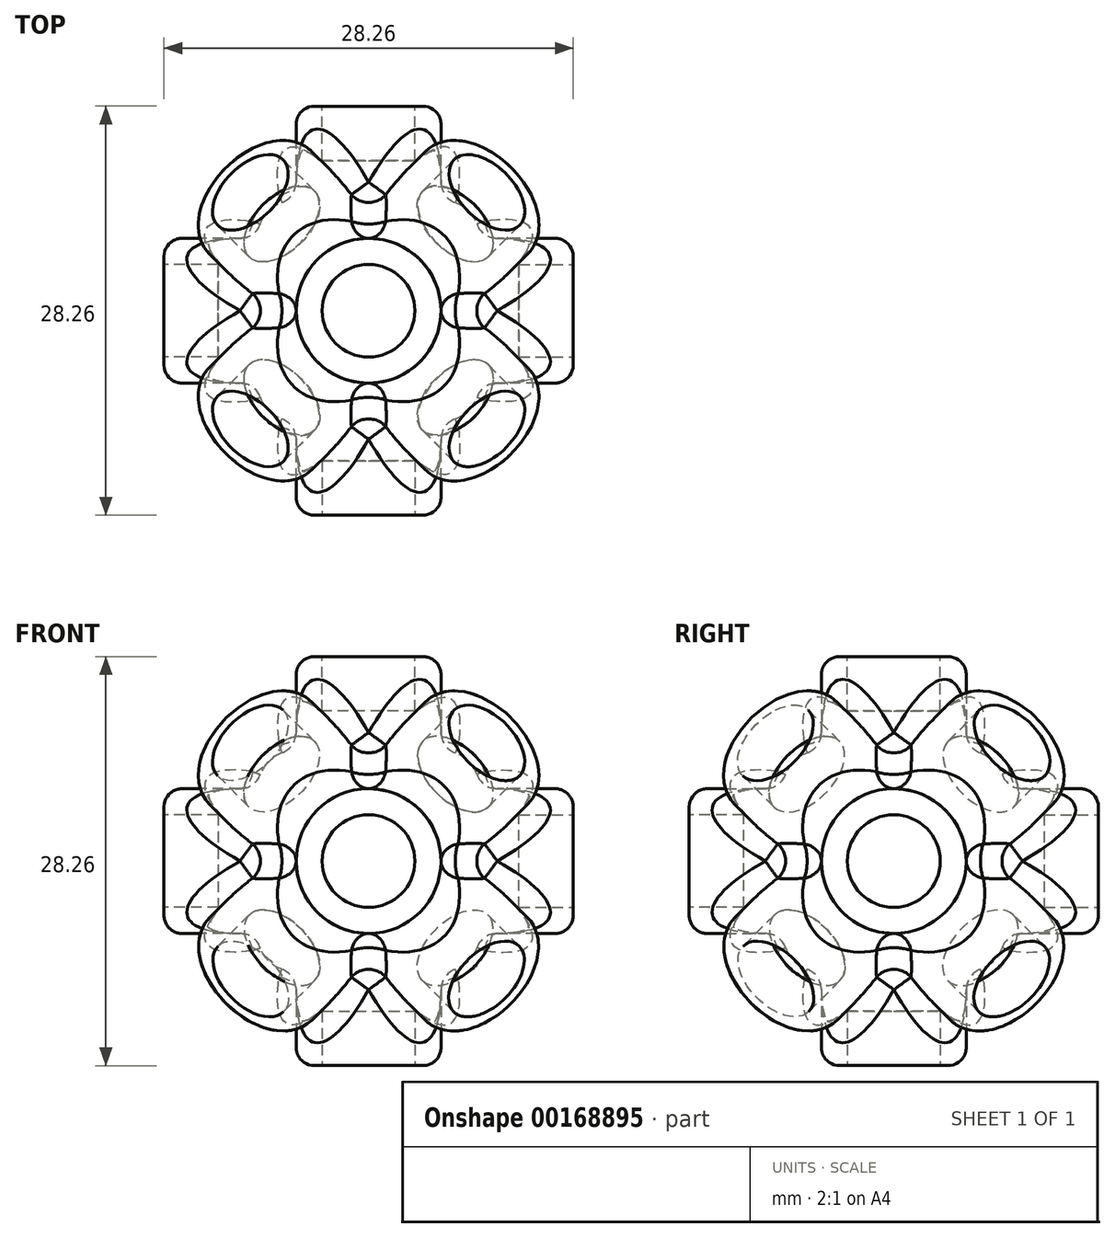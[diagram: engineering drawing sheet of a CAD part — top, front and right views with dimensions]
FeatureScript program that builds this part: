
annotation { "Feature Type Name" : "Feature", "Feature Type Description" : "" }
export const myFeature = defineFeature(function(context is Context, id is Id, definition is map)
    precondition{}
    {
        {
            var Q0;
            Q0=qCreatedBy(makeId("Top.planeOp"),FACE);
            var sketch = newSketch(context, id + "F0", { "sketchPlane" : qUnion([Q0])});
            skCircle(sketch, "E0", {"center": v(0, 0) * mm, "radius": 5 * mm});
            skSolve(sketch);
        }
        {
            var Q0;
            Q0=makeQuery(id+"F0.imprint","IMPRINT",FACE,{"disambiguationData":[TD([[makeQuery(id+"F0.imprint","IMPRINT",EDGE,{"derivedFrom":sQuery(id+"F0.wireOp",EDGE,"E0")}),1.0]])]});
            extrude(context, id + "F1", {"entities" : qUnion([Q0]), "endBound" : BoundingType.SYMMETRIC, "depth" : 28.25 * mm});
        }
        {
            var Q0;
            Q0=qCreatedBy(makeId("Right.planeOp"),FACE);
            var sketch = newSketch(context, id + "F2", { "sketchPlane" : qUnion([Q0])});
            skCircle(sketch, "E1", {"center": v(0, 0) * mm, "radius": 5 * mm});
            skSolve(sketch);
        }
        {
            var Q0;
            Q0=makeQuery(id+"F2.imprint","IMPRINT",FACE,{"disambiguationData":[TD([[makeQuery(id+"F2.imprint","IMPRINT",EDGE,{"derivedFrom":sQuery(id+"F2.wireOp",EDGE,"E1")}),1.0]])]});
            extrude(context, id + "F3", {"entities" : qUnion([Q0]), "operationType" : NewBodyOperationType.ADD, "endBound" : BoundingType.SYMMETRIC, "depth" : 28.25 * mm});
        }
        {
            var Q0;
            Q0=qCreatedBy(makeId("Front.planeOp"),FACE);
            var sketch = newSketch(context, id + "F4", { "sketchPlane" : qUnion([Q0])});
            skCircle(sketch, "E2", {"center": v(0, 0) * mm, "radius": 5 * mm});
            skSolve(sketch);
        }
        {
            var Q0;
            Q0=makeQuery(id+"F4.imprint","IMPRINT",FACE,{"disambiguationData":[TD([[makeQuery(id+"F4.imprint","IMPRINT",EDGE,{"derivedFrom":sQuery(id+"F4.wireOp",EDGE,"E2")}),1.0]])]});
            extrude(context, id + "F5", {"entities" : qUnion([Q0]), "operationType" : NewBodyOperationType.ADD, "endBound" : BoundingType.SYMMETRIC, "depth" : 28.25 * mm});
        }
        {
            var Q0;
            {var subQ0=sQuery(id+"F0.wireOp",EDGE,"E0");var subQ1=makeQuery(id+"F1.opExtrude","SWEPT_FACE",FACE,{"disambiguationData":[OSD([subQ0])]});Q0=makeQuery(id+"F5.boolean.opBoolean","INTERSECT",EDGE,{"disambiguationData":[OD(1.0)],"derivedFrom":[makeQuery(id+"F3.boolean.opBoolean","SPLIT",FACE,{"disambiguationData":[TD([makeQuery(id+"F1.opExtrude","CAP_FACE",FACE,{"disambiguationData":[OSD([subQ0])],"isStart":false})])],"derivedFrom":subQ1}),makeQuery(id+"F5.opExtrude","SWEPT_FACE",FACE,{"disambiguationData":[OSD([sQuery(id+"F4.wireOp",EDGE,"E2")])]})]});}
            cPoint(context, id + "F6", {"entities" : qUnion([Q0]), "parameter" : 0.5});
        }
        {
            var Q0;
            Q0=makeQuery(id+"F3.boolean.opBoolean","INTERSECT",EDGE,{"disambiguationData":[OD(3.0)],"derivedFrom":[makeQuery(id+"F1.opExtrude","SWEPT_FACE",FACE,{"disambiguationData":[OSD([sQuery(id+"F0.wireOp",EDGE,"E0")])]}),makeQuery(id+"F3.opExtrude","SWEPT_FACE",FACE,{"disambiguationData":[OSD([sQuery(id+"F2.wireOp",EDGE,"E1")])]})]});
            cPoint(context, id + "F7", {"entities" : qUnion([Q0]), "parameter" : 0.5});
        }
        {
            var Q0;
            {var subQ0=sQuery(id+"F2.wireOp",EDGE,"E1");var subQ1=makeQuery(id+"F3.opExtrude","SWEPT_FACE",FACE,{"disambiguationData":[OSD([subQ0])]});Q0=makeQuery(id+"F5.boolean.opBoolean","INTERSECT",EDGE,{"disambiguationData":[OD(1.0)],"derivedFrom":[makeQuery(id+"F3.boolean.opBoolean","SPLIT",FACE,{"disambiguationData":[TD([makeQuery(id+"F3.opExtrude","CAP_FACE",FACE,{"disambiguationData":[OSD([subQ0])],"isStart":false})])],"derivedFrom":subQ1}),makeQuery(id+"F5.opExtrude","SWEPT_FACE",FACE,{"disambiguationData":[OSD([sQuery(id+"F4.wireOp",EDGE,"E2")])]})]});}
            cPoint(context, id + "F8", {"entities" : qUnion([Q0]), "parameter" : 0.5});
        }
        {
            var Q0;
            Q0 = qCreatedBy(id + "F6" ,VERTEX);
            var Q1;
            Q1 = qCreatedBy(id + "F7" ,VERTEX);
            var Q2;
            Q2 = qCreatedBy(id + "F8" ,VERTEX);
            cPlane(context, id + "F9", {"entities" : qUnion([Q0, Q1, Q2]), "cplaneType" : CPlaneType.THREE_POINT, "offset" : 25 * mm, "width" : 150 * mm, "height" : 150 * mm});
        }
        {
            var Q0;
            {var subQ0=sQuery(id+"F0.wireOp",EDGE,"E0");var subQ1=makeQuery(id+"F1.opExtrude","SWEPT_FACE",FACE,{"disambiguationData":[OSD([subQ0])]});Q0=makeQuery(id+"F5.boolean.opBoolean","INTERSECT",EDGE,{"disambiguationData":[OD(1.0)],"derivedFrom":[makeQuery(id+"F3.boolean.opBoolean","SPLIT",FACE,{"disambiguationData":[TD([makeQuery(id+"F1.opExtrude","CAP_FACE",FACE,{"disambiguationData":[OSD([subQ0])],"isStart":false})])],"derivedFrom":subQ1}),makeQuery(id+"F5.opExtrude","SWEPT_FACE",FACE,{"disambiguationData":[OSD([sQuery(id+"F4.wireOp",EDGE,"E2")])]})]});}
            cPoint(context, id + "F10", {"entities" : qUnion([Q0]), "parameter" : 0.5});
        }
        {
            var Q0;
            Q0=makeQuery(id+"F3.boolean.opBoolean","INTERSECT",EDGE,{"disambiguationData":[OD(2.0)],"derivedFrom":[makeQuery(id+"F1.opExtrude","SWEPT_FACE",FACE,{"disambiguationData":[OSD([sQuery(id+"F0.wireOp",EDGE,"E0")])]}),makeQuery(id+"F3.opExtrude","SWEPT_FACE",FACE,{"disambiguationData":[OSD([sQuery(id+"F2.wireOp",EDGE,"E1")])]})]});
            cPoint(context, id + "F11", {"entities" : qUnion([Q0]), "parameter" : 0.5});
        }
        {
            var Q0;
            {var subQ0=sQuery(id+"F2.wireOp",EDGE,"E1");var subQ1=makeQuery(id+"F3.opExtrude","SWEPT_FACE",FACE,{"disambiguationData":[OSD([subQ0])]});Q0=makeQuery(id+"F5.boolean.opBoolean","INTERSECT",EDGE,{"disambiguationData":[OD(1.0)],"derivedFrom":[makeQuery(id+"F3.boolean.opBoolean","SPLIT",FACE,{"disambiguationData":[TD([makeQuery(id+"F3.opExtrude","CAP_FACE",FACE,{"disambiguationData":[OSD([subQ0])],"isStart":true})])],"derivedFrom":subQ1}),makeQuery(id+"F5.opExtrude","SWEPT_FACE",FACE,{"disambiguationData":[OSD([sQuery(id+"F4.wireOp",EDGE,"E2")])]})]});}
            cPoint(context, id + "F12", {"entities" : qUnion([Q0]), "parameter" : 0.5});
        }
        {
            var Q0;
            Q0 = qCreatedBy(id + "F10" ,VERTEX);
            var Q1;
            Q1 = qCreatedBy(id + "F11" ,VERTEX);
            var Q2;
            Q2 = qCreatedBy(id + "F12" ,VERTEX);
            cPlane(context, id + "F13", {"entities" : qUnion([Q0, Q1, Q2]), "cplaneType" : CPlaneType.THREE_POINT, "offset" : 25 * mm, "width" : 150 * mm, "height" : 150 * mm});
        }
        {
            var Q0;
            Q0=makeQuery(id+"F3.boolean.opBoolean","INTERSECT",EDGE,{"disambiguationData":[OD(2.0)],"derivedFrom":[makeQuery(id+"F1.opExtrude","SWEPT_FACE",FACE,{"disambiguationData":[OSD([sQuery(id+"F0.wireOp",EDGE,"E0")])]}),makeQuery(id+"F3.opExtrude","SWEPT_FACE",FACE,{"disambiguationData":[OSD([sQuery(id+"F2.wireOp",EDGE,"E1")])]})]});
            cPoint(context, id + "F14", {"entities" : qUnion([Q0]), "parameter" : 0.5});
        }
        {
            var Q0;
            {var subQ0=sQuery(id+"F0.wireOp",EDGE,"E0");var subQ1=makeQuery(id+"F1.opExtrude","SWEPT_FACE",FACE,{"disambiguationData":[OSD([subQ0])]});Q0=makeQuery(id+"F5.boolean.opBoolean","INTERSECT",EDGE,{"disambiguationData":[OD(0.0)],"derivedFrom":[makeQuery(id+"F3.boolean.opBoolean","SPLIT",FACE,{"disambiguationData":[TD([makeQuery(id+"F1.opExtrude","CAP_FACE",FACE,{"disambiguationData":[OSD([subQ0])],"isStart":false})])],"derivedFrom":subQ1}),makeQuery(id+"F5.opExtrude","SWEPT_FACE",FACE,{"disambiguationData":[OSD([sQuery(id+"F4.wireOp",EDGE,"E2")])]})]});}
            cPoint(context, id + "F15", {"entities" : qUnion([Q0]), "parameter" : 0.5});
        }
        {
            var Q0;
            {var subQ0=sQuery(id+"F2.wireOp",EDGE,"E1");var subQ1=makeQuery(id+"F3.opExtrude","SWEPT_FACE",FACE,{"disambiguationData":[OSD([subQ0])]});Q0=makeQuery(id+"F5.boolean.opBoolean","INTERSECT",EDGE,{"disambiguationData":[OD(0.0)],"derivedFrom":[makeQuery(id+"F3.boolean.opBoolean","SPLIT",FACE,{"disambiguationData":[TD([makeQuery(id+"F3.opExtrude","CAP_FACE",FACE,{"disambiguationData":[OSD([subQ0])],"isStart":true})])],"derivedFrom":subQ1}),makeQuery(id+"F5.opExtrude","SWEPT_FACE",FACE,{"disambiguationData":[OSD([sQuery(id+"F4.wireOp",EDGE,"E2")])]})]});}
            cPoint(context, id + "F16", {"entities" : qUnion([Q0]), "parameter" : 0.5});
        }
        {
            var Q0;
            Q0 = qCreatedBy(id + "F14" ,VERTEX);
            var Q1;
            Q1 = qCreatedBy(id + "F15" ,VERTEX);
            var Q2;
            Q2 = qCreatedBy(id + "F16" ,VERTEX);
            cPlane(context, id + "F17", {"entities" : qUnion([Q0, Q1, Q2]), "cplaneType" : CPlaneType.THREE_POINT, "offset" : 25 * mm, "width" : 150 * mm, "height" : 150 * mm});
        }
        {
            var Q0;
            Q0=makeQuery(id+"F3.boolean.opBoolean","INTERSECT",EDGE,{"disambiguationData":[OD(3.0)],"derivedFrom":[makeQuery(id+"F1.opExtrude","SWEPT_FACE",FACE,{"disambiguationData":[OSD([sQuery(id+"F0.wireOp",EDGE,"E0")])]}),makeQuery(id+"F3.opExtrude","SWEPT_FACE",FACE,{"disambiguationData":[OSD([sQuery(id+"F2.wireOp",EDGE,"E1")])]})]});
            cPoint(context, id + "F18", {"entities" : qUnion([Q0]), "parameter" : 0.5});
        }
        {
            var Q0;
            {var subQ0=sQuery(id+"F0.wireOp",EDGE,"E0");var subQ1=makeQuery(id+"F1.opExtrude","SWEPT_FACE",FACE,{"disambiguationData":[OSD([subQ0])]});Q0=makeQuery(id+"F5.boolean.opBoolean","INTERSECT",EDGE,{"disambiguationData":[OD(0.0)],"derivedFrom":[makeQuery(id+"F3.boolean.opBoolean","SPLIT",FACE,{"disambiguationData":[TD([makeQuery(id+"F1.opExtrude","CAP_FACE",FACE,{"disambiguationData":[OSD([subQ0])],"isStart":false})])],"derivedFrom":subQ1}),makeQuery(id+"F5.opExtrude","SWEPT_FACE",FACE,{"disambiguationData":[OSD([sQuery(id+"F4.wireOp",EDGE,"E2")])]})]});}
            cPoint(context, id + "F19", {"entities" : qUnion([Q0]), "parameter" : 0.5});
        }
        {
            var Q0;
            {var subQ0=sQuery(id+"F2.wireOp",EDGE,"E1");var subQ1=makeQuery(id+"F3.opExtrude","SWEPT_FACE",FACE,{"disambiguationData":[OSD([subQ0])]});Q0=makeQuery(id+"F5.boolean.opBoolean","INTERSECT",EDGE,{"disambiguationData":[OD(0.0)],"derivedFrom":[makeQuery(id+"F3.boolean.opBoolean","SPLIT",FACE,{"disambiguationData":[TD([makeQuery(id+"F3.opExtrude","CAP_FACE",FACE,{"disambiguationData":[OSD([subQ0])],"isStart":false})])],"derivedFrom":subQ1}),makeQuery(id+"F5.opExtrude","SWEPT_FACE",FACE,{"disambiguationData":[OSD([sQuery(id+"F4.wireOp",EDGE,"E2")])]})]});}
            cPoint(context, id + "F20", {"entities" : qUnion([Q0]), "parameter" : 0.5});
        }
        {
            var Q0;
            Q0 = qCreatedBy(id + "F18" ,VERTEX);
            var Q1;
            Q1 = qCreatedBy(id + "F19" ,VERTEX);
            var Q2;
            Q2 = qCreatedBy(id + "F20" ,VERTEX);
            cPlane(context, id + "F21", {"entities" : qUnion([Q0, Q1, Q2]), "cplaneType" : CPlaneType.THREE_POINT, "offset" : 25 * mm, "width" : 150 * mm, "height" : 150 * mm});
        }
        {
            var Q0;
            Q0=qCreatedBy(id+"F21.planeOp",FACE);
            cPlane(context, id + "F22", {"entities" : qUnion([Q0]), "cplaneType" : CPlaneType.OFFSET, "offset" : 5.75 * mm, "oppositeDirection" : true, "width" : 150 * mm, "height" : 150 * mm});
        }
        {
            var Q0;
            Q0=qCreatedBy(id+"F22.planeOp",FACE);
            var sketch = newSketch(context, id + "F23", { "sketchPlane" : qUnion([Q0])});
            skCircle(sketch, "E3", {"center": v(0, 0) * mm, "radius": 5 * mm});
            skSolve(sketch);
        }
        {
            var Q0;
            Q0=makeQuery(id+"F23.imprint","IMPRINT",FACE,{"disambiguationData":[TD([[makeQuery(id+"F23.imprint","IMPRINT",EDGE,{"derivedFrom":sQuery(id+"F23.wireOp",EDGE,"E3")}),1.0]])]});
            extrude(context, id + "F24", {"entities" : qUnion([Q0]), "operationType" : NewBodyOperationType.ADD, "endBound" : BoundingType.SYMMETRIC, "depth" : 28.25 * mm});
        }
        {
            var Q0;
            Q0=qCreatedBy(id+"F17.planeOp",FACE);
            cPlane(context, id + "F25", {"entities" : qUnion([Q0]), "cplaneType" : CPlaneType.OFFSET, "offset" : 5.75 * mm, "width" : 150 * mm, "height" : 150 * mm});
        }
        {
            var Q0;
            Q0=qCreatedBy(id+"F25.planeOp",FACE);
            var sketch = newSketch(context, id + "F26", { "sketchPlane" : qUnion([Q0])});
            skCircle(sketch, "E4", {"center": v(0, 0) * mm, "radius": 5 * mm});
            skSolve(sketch);
        }
        {
            var Q0;
            Q0=makeQuery(id+"F26.imprint","IMPRINT",FACE,{"disambiguationData":[TD([[makeQuery(id+"F26.imprint","IMPRINT",EDGE,{"derivedFrom":sQuery(id+"F26.wireOp",EDGE,"E4")}),1.0]])]});
            extrude(context, id + "F27", {"entities" : qUnion([Q0]), "operationType" : NewBodyOperationType.ADD, "endBound" : BoundingType.SYMMETRIC, "depth" : 28.25 * mm});
        }
        {
            var Q0;
            Q0=qCreatedBy(id+"F13.planeOp",FACE);
            cPlane(context, id + "F28", {"entities" : qUnion([Q0]), "cplaneType" : CPlaneType.OFFSET, "offset" : 5.75 * mm, "width" : 150 * mm, "height" : 150 * mm});
        }
        {
            var Q0;
            Q0=qCreatedBy(id+"F28.planeOp",FACE);
            var sketch = newSketch(context, id + "F29", { "sketchPlane" : qUnion([Q0])});
            skCircle(sketch, "E5", {"center": v(0, 0) * mm, "radius": 5 * mm});
            skSolve(sketch);
        }
        {
            var Q0;
            Q0=makeQuery(id+"F29.imprint","IMPRINT",FACE,{"disambiguationData":[TD([[makeQuery(id+"F29.imprint","IMPRINT",EDGE,{"derivedFrom":sQuery(id+"F29.wireOp",EDGE,"E5")}),1.0]])]});
            extrude(context, id + "F30", {"entities" : qUnion([Q0]), "operationType" : NewBodyOperationType.ADD, "endBound" : BoundingType.SYMMETRIC, "depth" : 28.25 * mm});
        }
        {
            var Q0;
            Q0=qCreatedBy(id+"F9.planeOp",FACE);
            cPlane(context, id + "F31", {"entities" : qUnion([Q0]), "cplaneType" : CPlaneType.OFFSET, "offset" : 5.75 * mm, "oppositeDirection" : true, "width" : 150 * mm, "height" : 150 * mm});
        }
        {
            var Q0;
            Q0=qCreatedBy(id+"F31.planeOp",FACE);
            var sketch = newSketch(context, id + "F32", { "sketchPlane" : qUnion([Q0])});
            skCircle(sketch, "E6", {"center": v(0, 0) * mm, "radius": 5 * mm});
            skSolve(sketch);
        }
        {
            var Q0;
            Q0=makeQuery(id+"F32.imprint","IMPRINT",FACE,{"disambiguationData":[TD([[makeQuery(id+"F32.imprint","IMPRINT",EDGE,{"derivedFrom":sQuery(id+"F32.wireOp",EDGE,"E6")}),1.0]])]});
            extrude(context, id + "F33", {"entities" : qUnion([Q0]), "operationType" : NewBodyOperationType.ADD, "endBound" : BoundingType.SYMMETRIC, "depth" : 28.25 * mm});
        }
        {
            var Q0;
            Q0=makeQuery(id+"F1.opExtrude","CAP_FACE",FACE,{"disambiguationData":[OSD([sQuery(id+"F0.wireOp",EDGE,"E0")])],"isStart":true});
            var Q1;
            Q1=makeQuery(id+"F27.opExtrude","CAP_FACE",FACE,{"disambiguationData":[OSD([sQuery(id+"F26.wireOp",EDGE,"E4")])],"isStart":false});
            var Q2;
            Q2=makeQuery(id+"F3.opExtrude","CAP_FACE",FACE,{"disambiguationData":[OSD([sQuery(id+"F2.wireOp",EDGE,"E1")])],"isStart":false});
            var Q3;
            Q3=makeQuery(id+"F30.opExtrude","CAP_FACE",FACE,{"disambiguationData":[OSD([sQuery(id+"F29.wireOp",EDGE,"E5")])],"isStart":false});
            var Q4;
            Q4=makeQuery(id+"F24.opExtrude","CAP_FACE",FACE,{"disambiguationData":[OSD([sQuery(id+"F23.wireOp",EDGE,"E3")])],"isStart":false});
            var Q5;
            Q5=makeQuery(id+"F5.opExtrude","CAP_FACE",FACE,{"disambiguationData":[OSD([sQuery(id+"F4.wireOp",EDGE,"E2")])],"isStart":true});
            var Q6;
            Q6=makeQuery(id+"F27.opExtrude","CAP_FACE",FACE,{"disambiguationData":[OSD([sQuery(id+"F26.wireOp",EDGE,"E4")])],"isStart":true});
            var Q7;
            Q7=makeQuery(id+"F3.opExtrude","CAP_FACE",FACE,{"disambiguationData":[OSD([sQuery(id+"F2.wireOp",EDGE,"E1")])],"isStart":true});
            var Q8;
            Q8=makeQuery(id+"F1.opExtrude","CAP_FACE",FACE,{"disambiguationData":[OSD([sQuery(id+"F0.wireOp",EDGE,"E0")])],"isStart":false});
            var Q9;
            Q9=makeQuery(id+"F30.opExtrude","CAP_FACE",FACE,{"disambiguationData":[OSD([sQuery(id+"F29.wireOp",EDGE,"E5")])],"isStart":true});
            var Q10;
            Q10=makeQuery(id+"F5.opExtrude","CAP_FACE",FACE,{"disambiguationData":[OSD([sQuery(id+"F4.wireOp",EDGE,"E2")])],"isStart":false});
            var Q11;
            Q11=makeQuery(id+"F33.opExtrude","CAP_FACE",FACE,{"disambiguationData":[OSD([sQuery(id+"F32.wireOp",EDGE,"E6")])],"isStart":false});
            var Q12;
            Q12=makeQuery(id+"F24.opExtrude","CAP_FACE",FACE,{"disambiguationData":[OSD([sQuery(id+"F23.wireOp",EDGE,"E3")])],"isStart":true});
            var Q13;
            Q13=makeQuery(id+"F33.opExtrude","CAP_FACE",FACE,{"disambiguationData":[OSD([sQuery(id+"F32.wireOp",EDGE,"E6")])],"isStart":true});
            fillet(context, id + "F34", {"entities" : qUnion([Q0, Q1, Q2, Q3, Q4, Q5, Q6, Q7, Q8, Q9, Q10, Q11, Q12, Q13]), "radius" : 1.25 * mm, "tangentPropagation" : true, "allowEdgeOverflow" : false});
        }
        {
            var Q0;
            Q0=makeQuery(id+"F3.opExtrude","CAP_FACE",FACE,{"disambiguationData":[OSD([sQuery(id+"F2.wireOp",EDGE,"E1")])],"isStart":false});
            var sketch = newSketch(context, id + "F35", { "sketchPlane" : qUnion([Q0])});
            skCircle(sketch, "E7", {"center": v(0, 0) * mm, "radius": 3.2 * mm});
            skSolve(sketch);
        }
        {
            var Q0;
            Q0=makeQuery(id+"F33.opExtrude","CAP_FACE",FACE,{"disambiguationData":[OSD([sQuery(id+"F32.wireOp",EDGE,"E6")])],"isStart":false});
            var sketch = newSketch(context, id + "F36", { "sketchPlane" : qUnion([Q0])});
            skCircle(sketch, "E8", {"center": v(0, 0) * mm, "radius": 3.2 * mm});
            skSolve(sketch);
        }
        {
            var Q0;
            Q0=makeQuery(id+"F35.imprint","IMPRINT",FACE,{"disambiguationData":[TD([[makeQuery(id+"F35.imprint","IMPRINT",EDGE,{"derivedFrom":sQuery(id+"F35.wireOp",EDGE,"E7")}),1.0]])]});
            extrude(context, id + "F37", {"entities" : qUnion([Q0]), "operationType" : NewBodyOperationType.REMOVE, "oppositeDirection" : true, "depth" : 3.75 * mm});
        }
        {
            var Q0;
            Q0=makeQuery(id+"F36.imprint","IMPRINT",FACE,{"disambiguationData":[TD([[makeQuery(id+"F36.imprint","IMPRINT",EDGE,{"derivedFrom":sQuery(id+"F36.wireOp",EDGE,"E8")}),1.0]])]});
            extrude(context, id + "F38", {"entities" : qUnion([Q0]), "operationType" : NewBodyOperationType.REMOVE, "oppositeDirection" : true, "depth" : 3.75 * mm});
        }
        {
            var Q0;
            Q0=makeQuery(id+"F30.opExtrude","CAP_FACE",FACE,{"disambiguationData":[OSD([sQuery(id+"F29.wireOp",EDGE,"E5")])],"isStart":false});
            var sketch = newSketch(context, id + "F39", { "sketchPlane" : qUnion([Q0])});
            skCircle(sketch, "E9", {"center": v(0, 0) * mm, "radius": 3.2 * mm});
            skSolve(sketch);
        }
        {
            var Q0;
            Q0=makeQuery(id+"F39.imprint","IMPRINT",FACE,{"disambiguationData":[TD([[makeQuery(id+"F39.imprint","IMPRINT",EDGE,{"derivedFrom":sQuery(id+"F39.wireOp",EDGE,"E9")}),1.0]])]});
            extrude(context, id + "F40", {"entities" : qUnion([Q0]), "operationType" : NewBodyOperationType.REMOVE, "oppositeDirection" : true, "depth" : 3.75 * mm});
        }
        {
            var Q0;
            Q0=makeQuery(id+"F27.opExtrude","CAP_FACE",FACE,{"disambiguationData":[OSD([sQuery(id+"F26.wireOp",EDGE,"E4")])],"isStart":false});
            var sketch = newSketch(context, id + "F41", { "sketchPlane" : qUnion([Q0])});
            skCircle(sketch, "E10", {"center": v(0, 0) * mm, "radius": 3.2 * mm});
            skSolve(sketch);
        }
        {
            var Q0;
            Q0=makeQuery(id+"F41.imprint","IMPRINT",FACE,{"disambiguationData":[TD([[makeQuery(id+"F41.imprint","IMPRINT",EDGE,{"derivedFrom":sQuery(id+"F41.wireOp",EDGE,"E10")}),1.0]])]});
            extrude(context, id + "F42", {"entities" : qUnion([Q0]), "operationType" : NewBodyOperationType.REMOVE, "oppositeDirection" : true, "depth" : 3.75 * mm});
        }
        {
            var Q0;
            Q0=makeQuery(id+"F1.opExtrude","CAP_FACE",FACE,{"disambiguationData":[OSD([sQuery(id+"F0.wireOp",EDGE,"E0")])],"isStart":true});
            var sketch = newSketch(context, id + "F43", { "sketchPlane" : qUnion([Q0])});
            skCircle(sketch, "E11", {"center": v(0, 0) * mm, "radius": 3.2 * mm});
            skSolve(sketch);
        }
        {
            var Q0;
            Q0=makeQuery(id+"F43.imprint","IMPRINT",FACE,{"disambiguationData":[TD([[makeQuery(id+"F43.imprint","IMPRINT",EDGE,{"derivedFrom":sQuery(id+"F43.wireOp",EDGE,"E11")}),1.0]])]});
            extrude(context, id + "F44", {"entities" : qUnion([Q0]), "operationType" : NewBodyOperationType.REMOVE, "oppositeDirection" : true, "depth" : 3.75 * mm});
        }
        {
            var Q0;
            Q0=makeQuery(id+"F5.opExtrude","CAP_FACE",FACE,{"disambiguationData":[OSD([sQuery(id+"F4.wireOp",EDGE,"E2")])],"isStart":false});
            var sketch = newSketch(context, id + "F45", { "sketchPlane" : qUnion([Q0])});
            skCircle(sketch, "E12", {"center": v(0, 0) * mm, "radius": 3.2 * mm});
            skSolve(sketch);
        }
        {
            var Q0;
            Q0=makeQuery(id+"F45.imprint","IMPRINT",FACE,{"disambiguationData":[TD([[makeQuery(id+"F45.imprint","IMPRINT",EDGE,{"derivedFrom":sQuery(id+"F45.wireOp",EDGE,"E12")}),1.0]])]});
            extrude(context, id + "F46", {"entities" : qUnion([Q0]), "operationType" : NewBodyOperationType.REMOVE, "oppositeDirection" : true, "depth" : 3.75 * mm});
        }
        {
            var Q0;
            Q0=makeQuery(id+"F24.opExtrude","CAP_FACE",FACE,{"disambiguationData":[OSD([sQuery(id+"F23.wireOp",EDGE,"E3")])],"isStart":true});
            var sketch = newSketch(context, id + "F47", { "sketchPlane" : qUnion([Q0])});
            skCircle(sketch, "E13", {"center": v(0, 0) * mm, "radius": 3.2 * mm});
            skSolve(sketch);
        }
        {
            var Q0;
            Q0=makeQuery(id+"F47.imprint","IMPRINT",FACE,{"disambiguationData":[TD([[makeQuery(id+"F47.imprint","IMPRINT",EDGE,{"derivedFrom":sQuery(id+"F47.wireOp",EDGE,"E13")}),1.0]])]});
            extrude(context, id + "F48", {"entities" : qUnion([Q0]), "operationType" : NewBodyOperationType.REMOVE, "oppositeDirection" : true, "depth" : 3.75 * mm});
        }
        {
            var Q0;
            Q0=makeQuery(id+"F24.opExtrude","CAP_FACE",FACE,{"disambiguationData":[OSD([sQuery(id+"F23.wireOp",EDGE,"E3")])],"isStart":false});
            var sketch = newSketch(context, id + "F49", { "sketchPlane" : qUnion([Q0])});
            skCircle(sketch, "E14", {"center": v(0, 0) * mm, "radius": 3.2 * mm});
            skSolve(sketch);
        }
        {
            var Q0;
            Q0=makeQuery(id+"F49.imprint","IMPRINT",FACE,{"disambiguationData":[TD([[makeQuery(id+"F49.imprint","IMPRINT",EDGE,{"derivedFrom":sQuery(id+"F49.wireOp",EDGE,"E14")}),1.0]])]});
            extrude(context, id + "F50", {"entities" : qUnion([Q0]), "operationType" : NewBodyOperationType.REMOVE, "oppositeDirection" : true, "depth" : 3.75 * mm});
        }
        {
            var Q0;
            Q0=makeQuery(id+"F5.opExtrude","CAP_FACE",FACE,{"disambiguationData":[OSD([sQuery(id+"F4.wireOp",EDGE,"E2")])],"isStart":true});
            var sketch = newSketch(context, id + "F51", { "sketchPlane" : qUnion([Q0])});
            skCircle(sketch, "E15", {"center": v(0, 0) * mm, "radius": 3.2 * mm});
            skSolve(sketch);
        }
        {
            var Q0;
            Q0=makeQuery(id+"F51.imprint","IMPRINT",FACE,{"disambiguationData":[TD([[makeQuery(id+"F51.imprint","IMPRINT",EDGE,{"derivedFrom":sQuery(id+"F51.wireOp",EDGE,"E15")}),1.0]])]});
            extrude(context, id + "F52", {"entities" : qUnion([Q0]), "operationType" : NewBodyOperationType.REMOVE, "oppositeDirection" : true, "depth" : 3.75 * mm});
        }
        {
            var Q0;
            Q0=makeQuery(id+"F27.opExtrude","CAP_FACE",FACE,{"disambiguationData":[OSD([sQuery(id+"F26.wireOp",EDGE,"E4")])],"isStart":true});
            var sketch = newSketch(context, id + "F53", { "sketchPlane" : qUnion([Q0])});
            skCircle(sketch, "E16", {"center": v(0, 0) * mm, "radius": 3.2 * mm});
            skSolve(sketch);
        }
        {
            var Q0;
            Q0=makeQuery(id+"F53.imprint","IMPRINT",FACE,{"disambiguationData":[TD([[makeQuery(id+"F53.imprint","IMPRINT",EDGE,{"derivedFrom":sQuery(id+"F53.wireOp",EDGE,"E16")}),1.0]])]});
            extrude(context, id + "F54", {"entities" : qUnion([Q0]), "operationType" : NewBodyOperationType.REMOVE, "oppositeDirection" : true, "depth" : 3.75 * mm});
        }
        {
            var Q0;
            Q0=makeQuery(id+"F1.opExtrude","CAP_FACE",FACE,{"disambiguationData":[OSD([sQuery(id+"F0.wireOp",EDGE,"E0")])],"isStart":false});
            var sketch = newSketch(context, id + "F55", { "sketchPlane" : qUnion([Q0])});
            skCircle(sketch, "E17", {"center": v(0, 0) * mm, "radius": 3.2 * mm});
            skSolve(sketch);
        }
        {
            var Q0;
            Q0=makeQuery(id+"F55.imprint","IMPRINT",FACE,{"disambiguationData":[TD([[makeQuery(id+"F55.imprint","IMPRINT",EDGE,{"derivedFrom":sQuery(id+"F55.wireOp",EDGE,"E17")}),1.0]])]});
            extrude(context, id + "F56", {"entities" : qUnion([Q0]), "operationType" : NewBodyOperationType.REMOVE, "oppositeDirection" : true, "depth" : 3.75 * mm});
        }
        {
            var Q0;
            Q0=makeQuery(id+"F3.opExtrude","CAP_FACE",FACE,{"disambiguationData":[OSD([sQuery(id+"F2.wireOp",EDGE,"E1")])],"isStart":true});
            var sketch = newSketch(context, id + "F57", { "sketchPlane" : qUnion([Q0])});
            skCircle(sketch, "E18", {"center": v(0, 0) * mm, "radius": 3.2 * mm});
            skSolve(sketch);
        }
        {
            var Q0;
            Q0=makeQuery(id+"F57.imprint","IMPRINT",FACE,{"disambiguationData":[TD([[makeQuery(id+"F57.imprint","IMPRINT",EDGE,{"derivedFrom":sQuery(id+"F57.wireOp",EDGE,"E18")}),1.0]])]});
            extrude(context, id + "F58", {"entities" : qUnion([Q0]), "operationType" : NewBodyOperationType.REMOVE, "oppositeDirection" : true, "depth" : 3.75 * mm});
        }
        {
            var Q0;
            Q0=makeQuery(id+"F33.opExtrude","CAP_FACE",FACE,{"disambiguationData":[OSD([sQuery(id+"F32.wireOp",EDGE,"E6")])],"isStart":true});
            var sketch = newSketch(context, id + "F59", { "sketchPlane" : qUnion([Q0])});
            skCircle(sketch, "E19", {"center": v(0, 0) * mm, "radius": 3.2 * mm});
            skSolve(sketch);
        }
        {
            var Q0;
            Q0=makeQuery(id+"F59.imprint","IMPRINT",FACE,{"disambiguationData":[TD([[makeQuery(id+"F59.imprint","IMPRINT",EDGE,{"derivedFrom":sQuery(id+"F59.wireOp",EDGE,"E19")}),1.0]])]});
            extrude(context, id + "F60", {"entities" : qUnion([Q0]), "operationType" : NewBodyOperationType.REMOVE, "oppositeDirection" : true, "depth" : 3.75 * mm});
        }
        {
            var Q0;
            Q0=makeQuery(id+"F30.opExtrude","CAP_FACE",FACE,{"disambiguationData":[OSD([sQuery(id+"F29.wireOp",EDGE,"E5")])],"isStart":true});
            var sketch = newSketch(context, id + "F61", { "sketchPlane" : qUnion([Q0])});
            skCircle(sketch, "E20", {"center": v(0, 0) * mm, "radius": 3.2 * mm});
            skSolve(sketch);
        }
        {
            var Q0;
            Q0=makeQuery(id+"F61.imprint","IMPRINT",FACE,{"disambiguationData":[TD([[makeQuery(id+"F61.imprint","IMPRINT",EDGE,{"derivedFrom":sQuery(id+"F61.wireOp",EDGE,"E20")}),1.0]])]});
            extrude(context, id + "F62", {"entities" : qUnion([Q0]), "operationType" : NewBodyOperationType.REMOVE, "oppositeDirection" : true, "depth" : 3.75 * mm});
        }
        {
            var Q0;
            {var subQ0=sQuery(id+"F0.wireOp",EDGE,"E0");var subQ1=makeQuery(id+"F1.opExtrude","SWEPT_FACE",FACE,{"disambiguationData":[OSD([subQ0])]});Q0=makeQuery(id+"F33.boolean.opBoolean","INTERSECT",EDGE,{"derivedFrom":[makeQuery(id+"F3.boolean.opBoolean","SPLIT",FACE,{"disambiguationData":[TD([makeQuery(id+"F1.opExtrude","CAP_FACE",FACE,{"disambiguationData":[OSD([subQ0])],"isStart":true})])],"derivedFrom":subQ1}),makeQuery(id+"F33.opExtrude","SWEPT_FACE",FACE,{"disambiguationData":[OSD([sQuery(id+"F32.wireOp",EDGE,"E6")])]})]});}
            var Q1;
            {var subQ0=sQuery(id+"F2.wireOp",EDGE,"E1");var subQ1=makeQuery(id+"F3.opExtrude","SWEPT_FACE",FACE,{"disambiguationData":[OSD([subQ0])]});Q1=makeQuery(id+"F33.boolean.opBoolean","INTERSECT",EDGE,{"derivedFrom":[makeQuery(id+"F3.boolean.opBoolean","SPLIT",FACE,{"disambiguationData":[TD([makeQuery(id+"F3.opExtrude","CAP_FACE",FACE,{"disambiguationData":[OSD([subQ0])],"isStart":true})])],"derivedFrom":subQ1}),makeQuery(id+"F33.opExtrude","SWEPT_FACE",FACE,{"disambiguationData":[OSD([sQuery(id+"F32.wireOp",EDGE,"E6")])]})]});}
            var Q2;
            {var subQ0=sQuery(id+"F4.wireOp",EDGE,"E2");Q2=makeQuery(id+"F24.boolean.opBoolean","INTERSECT",EDGE,{"derivedFrom":[makeQuery(id+"F5.boolean.opBoolean","SPLIT",FACE,{"disambiguationData":[TD([makeQuery(id+"F5.opExtrude","CAP_FACE",FACE,{"disambiguationData":[OSD([subQ0])],"isStart":false})])],"derivedFrom":makeQuery(id+"F5.opExtrude","SWEPT_FACE",FACE,{"disambiguationData":[OSD([subQ0])]})}),makeQuery(id+"F24.opExtrude","SWEPT_FACE",FACE,{"disambiguationData":[OSD([sQuery(id+"F23.wireOp",EDGE,"E3")])]})]});}
            var Q3;
            {var subQ0=sQuery(id+"F4.wireOp",EDGE,"E2");Q3=makeQuery(id+"F30.boolean.opBoolean","INTERSECT",EDGE,{"derivedFrom":[makeQuery(id+"F5.boolean.opBoolean","SPLIT",FACE,{"disambiguationData":[TD([makeQuery(id+"F5.opExtrude","CAP_FACE",FACE,{"disambiguationData":[OSD([subQ0])],"isStart":false})])],"derivedFrom":makeQuery(id+"F5.opExtrude","SWEPT_FACE",FACE,{"disambiguationData":[OSD([subQ0])]})}),makeQuery(id+"F30.opExtrude","SWEPT_FACE",FACE,{"disambiguationData":[OSD([sQuery(id+"F29.wireOp",EDGE,"E5")])]})]});}
            var Q4;
            {var subQ0=sQuery(id+"F4.wireOp",EDGE,"E2");Q4=makeQuery(id+"F33.boolean.opBoolean","INTERSECT",EDGE,{"derivedFrom":[makeQuery(id+"F5.boolean.opBoolean","SPLIT",FACE,{"disambiguationData":[TD([makeQuery(id+"F5.opExtrude","CAP_FACE",FACE,{"disambiguationData":[OSD([subQ0])],"isStart":false})])],"derivedFrom":makeQuery(id+"F5.opExtrude","SWEPT_FACE",FACE,{"disambiguationData":[OSD([subQ0])]})}),makeQuery(id+"F33.opExtrude","SWEPT_FACE",FACE,{"disambiguationData":[OSD([sQuery(id+"F32.wireOp",EDGE,"E6")])]})]});}
            var Q5;
            {var subQ0=sQuery(id+"F4.wireOp",EDGE,"E2");Q5=makeQuery(id+"F27.boolean.opBoolean","INTERSECT",EDGE,{"derivedFrom":[makeQuery(id+"F5.boolean.opBoolean","SPLIT",FACE,{"disambiguationData":[TD([makeQuery(id+"F5.opExtrude","CAP_FACE",FACE,{"disambiguationData":[OSD([subQ0])],"isStart":false})])],"derivedFrom":makeQuery(id+"F5.opExtrude","SWEPT_FACE",FACE,{"disambiguationData":[OSD([subQ0])]})}),makeQuery(id+"F27.opExtrude","SWEPT_FACE",FACE,{"disambiguationData":[OSD([sQuery(id+"F26.wireOp",EDGE,"E4")])]})]});}
            var Q6;
            {var subQ0=sQuery(id+"F2.wireOp",EDGE,"E1");var subQ1=makeQuery(id+"F3.opExtrude","SWEPT_FACE",FACE,{"disambiguationData":[OSD([subQ0])]});Q6=makeQuery(id+"F33.boolean.opBoolean","INTERSECT",EDGE,{"derivedFrom":[makeQuery(id+"F3.boolean.opBoolean","SPLIT",FACE,{"disambiguationData":[TD([makeQuery(id+"F3.opExtrude","CAP_FACE",FACE,{"disambiguationData":[OSD([subQ0])],"isStart":false})])],"derivedFrom":subQ1}),makeQuery(id+"F33.opExtrude","SWEPT_FACE",FACE,{"disambiguationData":[OSD([sQuery(id+"F32.wireOp",EDGE,"E6")])]})]});}
            var Q7;
            {var subQ0=sQuery(id+"F2.wireOp",EDGE,"E1");var subQ1=makeQuery(id+"F3.opExtrude","SWEPT_FACE",FACE,{"disambiguationData":[OSD([subQ0])]});Q7=makeQuery(id+"F27.boolean.opBoolean","INTERSECT",EDGE,{"derivedFrom":[makeQuery(id+"F3.boolean.opBoolean","SPLIT",FACE,{"disambiguationData":[TD([makeQuery(id+"F3.opExtrude","CAP_FACE",FACE,{"disambiguationData":[OSD([subQ0])],"isStart":false})])],"derivedFrom":subQ1}),makeQuery(id+"F27.opExtrude","SWEPT_FACE",FACE,{"disambiguationData":[OSD([sQuery(id+"F26.wireOp",EDGE,"E4")])]})]});}
            var Q8;
            {var subQ0=sQuery(id+"F0.wireOp",EDGE,"E0");var subQ1=makeQuery(id+"F1.opExtrude","SWEPT_FACE",FACE,{"disambiguationData":[OSD([subQ0])]});Q8=makeQuery(id+"F27.boolean.opBoolean","INTERSECT",EDGE,{"derivedFrom":[makeQuery(id+"F3.boolean.opBoolean","SPLIT",FACE,{"disambiguationData":[TD([makeQuery(id+"F1.opExtrude","CAP_FACE",FACE,{"disambiguationData":[OSD([subQ0])],"isStart":true})])],"derivedFrom":subQ1}),makeQuery(id+"F27.opExtrude","SWEPT_FACE",FACE,{"disambiguationData":[OSD([sQuery(id+"F26.wireOp",EDGE,"E4")])]})]});}
            var Q9;
            {var subQ0=sQuery(id+"F0.wireOp",EDGE,"E0");var subQ1=makeQuery(id+"F1.opExtrude","SWEPT_FACE",FACE,{"disambiguationData":[OSD([subQ0])]});Q9=makeQuery(id+"F24.boolean.opBoolean","INTERSECT",EDGE,{"derivedFrom":[makeQuery(id+"F3.boolean.opBoolean","SPLIT",FACE,{"disambiguationData":[TD([makeQuery(id+"F1.opExtrude","CAP_FACE",FACE,{"disambiguationData":[OSD([subQ0])],"isStart":true})])],"derivedFrom":subQ1}),makeQuery(id+"F24.opExtrude","SWEPT_FACE",FACE,{"disambiguationData":[OSD([sQuery(id+"F23.wireOp",EDGE,"E3")])]})]});}
            var Q10;
            {var subQ0=sQuery(id+"F2.wireOp",EDGE,"E1");var subQ1=makeQuery(id+"F3.opExtrude","SWEPT_FACE",FACE,{"disambiguationData":[OSD([subQ0])]});Q10=makeQuery(id+"F24.boolean.opBoolean","INTERSECT",EDGE,{"derivedFrom":[makeQuery(id+"F3.boolean.opBoolean","SPLIT",FACE,{"disambiguationData":[TD([makeQuery(id+"F3.opExtrude","CAP_FACE",FACE,{"disambiguationData":[OSD([subQ0])],"isStart":true})])],"derivedFrom":subQ1}),makeQuery(id+"F24.opExtrude","SWEPT_FACE",FACE,{"disambiguationData":[OSD([sQuery(id+"F23.wireOp",EDGE,"E3")])]})]});}
            var Q11;
            {var subQ0=sQuery(id+"F0.wireOp",EDGE,"E0");var subQ1=makeQuery(id+"F1.opExtrude","SWEPT_FACE",FACE,{"disambiguationData":[OSD([subQ0])]});Q11=makeQuery(id+"F30.boolean.opBoolean","INTERSECT",EDGE,{"derivedFrom":[makeQuery(id+"F3.boolean.opBoolean","SPLIT",FACE,{"disambiguationData":[TD([makeQuery(id+"F1.opExtrude","CAP_FACE",FACE,{"disambiguationData":[OSD([subQ0])],"isStart":false})])],"derivedFrom":subQ1}),makeQuery(id+"F30.opExtrude","SWEPT_FACE",FACE,{"disambiguationData":[OSD([sQuery(id+"F29.wireOp",EDGE,"E5")])]})]});}
            var Q12;
            {var subQ0=sQuery(id+"F0.wireOp",EDGE,"E0");var subQ1=makeQuery(id+"F1.opExtrude","SWEPT_FACE",FACE,{"disambiguationData":[OSD([subQ0])]});Q12=makeQuery(id+"F33.boolean.opBoolean","INTERSECT",EDGE,{"derivedFrom":[makeQuery(id+"F3.boolean.opBoolean","SPLIT",FACE,{"disambiguationData":[TD([makeQuery(id+"F1.opExtrude","CAP_FACE",FACE,{"disambiguationData":[OSD([subQ0])],"isStart":false})])],"derivedFrom":subQ1}),makeQuery(id+"F33.opExtrude","SWEPT_FACE",FACE,{"disambiguationData":[OSD([sQuery(id+"F32.wireOp",EDGE,"E6")])]})]});}
            var Q13;
            {var subQ0=sQuery(id+"F0.wireOp",EDGE,"E0");var subQ1=makeQuery(id+"F1.opExtrude","SWEPT_FACE",FACE,{"disambiguationData":[OSD([subQ0])]});Q13=makeQuery(id+"F27.boolean.opBoolean","INTERSECT",EDGE,{"derivedFrom":[makeQuery(id+"F3.boolean.opBoolean","SPLIT",FACE,{"disambiguationData":[TD([makeQuery(id+"F1.opExtrude","CAP_FACE",FACE,{"disambiguationData":[OSD([subQ0])],"isStart":false})])],"derivedFrom":subQ1}),makeQuery(id+"F27.opExtrude","SWEPT_FACE",FACE,{"disambiguationData":[OSD([sQuery(id+"F26.wireOp",EDGE,"E4")])]})]});}
            var Q14;
            {var subQ0=sQuery(id+"F2.wireOp",EDGE,"E1");var subQ1=makeQuery(id+"F3.opExtrude","SWEPT_FACE",FACE,{"disambiguationData":[OSD([subQ0])]});Q14=makeQuery(id+"F30.boolean.opBoolean","INTERSECT",EDGE,{"derivedFrom":[makeQuery(id+"F3.boolean.opBoolean","SPLIT",FACE,{"disambiguationData":[TD([makeQuery(id+"F3.opExtrude","CAP_FACE",FACE,{"disambiguationData":[OSD([subQ0])],"isStart":true})])],"derivedFrom":subQ1}),makeQuery(id+"F30.opExtrude","SWEPT_FACE",FACE,{"disambiguationData":[OSD([sQuery(id+"F29.wireOp",EDGE,"E5")])]})]});}
            var Q15;
            {var subQ0=sQuery(id+"F2.wireOp",EDGE,"E1");var subQ1=makeQuery(id+"F3.opExtrude","SWEPT_FACE",FACE,{"disambiguationData":[OSD([subQ0])]});Q15=makeQuery(id+"F27.boolean.opBoolean","INTERSECT",EDGE,{"derivedFrom":[makeQuery(id+"F3.boolean.opBoolean","SPLIT",FACE,{"disambiguationData":[TD([makeQuery(id+"F3.opExtrude","CAP_FACE",FACE,{"disambiguationData":[OSD([subQ0])],"isStart":true})])],"derivedFrom":subQ1}),makeQuery(id+"F27.opExtrude","SWEPT_FACE",FACE,{"disambiguationData":[OSD([sQuery(id+"F26.wireOp",EDGE,"E4")])]})]});}
            var Q16;
            {var subQ0=sQuery(id+"F4.wireOp",EDGE,"E2");Q16=makeQuery(id+"F33.boolean.opBoolean","INTERSECT",EDGE,{"derivedFrom":[makeQuery(id+"F5.boolean.opBoolean","SPLIT",FACE,{"disambiguationData":[TD([makeQuery(id+"F5.opExtrude","CAP_FACE",FACE,{"disambiguationData":[OSD([subQ0])],"isStart":true})])],"derivedFrom":makeQuery(id+"F5.opExtrude","SWEPT_FACE",FACE,{"disambiguationData":[OSD([subQ0])]})}),makeQuery(id+"F33.opExtrude","SWEPT_FACE",FACE,{"disambiguationData":[OSD([sQuery(id+"F32.wireOp",EDGE,"E6")])]})]});}
            var Q17;
            {var subQ0=sQuery(id+"F4.wireOp",EDGE,"E2");Q17=makeQuery(id+"F27.boolean.opBoolean","INTERSECT",EDGE,{"derivedFrom":[makeQuery(id+"F5.boolean.opBoolean","SPLIT",FACE,{"disambiguationData":[TD([makeQuery(id+"F5.opExtrude","CAP_FACE",FACE,{"disambiguationData":[OSD([subQ0])],"isStart":true})])],"derivedFrom":makeQuery(id+"F5.opExtrude","SWEPT_FACE",FACE,{"disambiguationData":[OSD([subQ0])]})}),makeQuery(id+"F27.opExtrude","SWEPT_FACE",FACE,{"disambiguationData":[OSD([sQuery(id+"F26.wireOp",EDGE,"E4")])]})]});}
            var Q18;
            {var subQ0=sQuery(id+"F4.wireOp",EDGE,"E2");Q18=makeQuery(id+"F24.boolean.opBoolean","INTERSECT",EDGE,{"derivedFrom":[makeQuery(id+"F5.boolean.opBoolean","SPLIT",FACE,{"disambiguationData":[TD([makeQuery(id+"F5.opExtrude","CAP_FACE",FACE,{"disambiguationData":[OSD([subQ0])],"isStart":true})])],"derivedFrom":makeQuery(id+"F5.opExtrude","SWEPT_FACE",FACE,{"disambiguationData":[OSD([subQ0])]})}),makeQuery(id+"F24.opExtrude","SWEPT_FACE",FACE,{"disambiguationData":[OSD([sQuery(id+"F23.wireOp",EDGE,"E3")])]})]});}
            var Q19;
            {var subQ0=sQuery(id+"F0.wireOp",EDGE,"E0");var subQ1=makeQuery(id+"F1.opExtrude","SWEPT_FACE",FACE,{"disambiguationData":[OSD([subQ0])]});Q19=makeQuery(id+"F24.boolean.opBoolean","INTERSECT",EDGE,{"derivedFrom":[makeQuery(id+"F3.boolean.opBoolean","SPLIT",FACE,{"disambiguationData":[TD([makeQuery(id+"F1.opExtrude","CAP_FACE",FACE,{"disambiguationData":[OSD([subQ0])],"isStart":false})])],"derivedFrom":subQ1}),makeQuery(id+"F24.opExtrude","SWEPT_FACE",FACE,{"disambiguationData":[OSD([sQuery(id+"F23.wireOp",EDGE,"E3")])]})]});}
            var Q20;
            {var subQ0=sQuery(id+"F2.wireOp",EDGE,"E1");var subQ1=makeQuery(id+"F3.opExtrude","SWEPT_FACE",FACE,{"disambiguationData":[OSD([subQ0])]});Q20=makeQuery(id+"F30.boolean.opBoolean","INTERSECT",EDGE,{"derivedFrom":[makeQuery(id+"F3.boolean.opBoolean","SPLIT",FACE,{"disambiguationData":[TD([makeQuery(id+"F3.opExtrude","CAP_FACE",FACE,{"disambiguationData":[OSD([subQ0])],"isStart":false})])],"derivedFrom":subQ1}),makeQuery(id+"F30.opExtrude","SWEPT_FACE",FACE,{"disambiguationData":[OSD([sQuery(id+"F29.wireOp",EDGE,"E5")])]})]});}
            var Q21;
            {var subQ0=sQuery(id+"F2.wireOp",EDGE,"E1");var subQ1=makeQuery(id+"F3.opExtrude","SWEPT_FACE",FACE,{"disambiguationData":[OSD([subQ0])]});Q21=makeQuery(id+"F24.boolean.opBoolean","INTERSECT",EDGE,{"derivedFrom":[makeQuery(id+"F3.boolean.opBoolean","SPLIT",FACE,{"disambiguationData":[TD([makeQuery(id+"F3.opExtrude","CAP_FACE",FACE,{"disambiguationData":[OSD([subQ0])],"isStart":false})])],"derivedFrom":subQ1}),makeQuery(id+"F24.opExtrude","SWEPT_FACE",FACE,{"disambiguationData":[OSD([sQuery(id+"F23.wireOp",EDGE,"E3")])]})]});}
            var Q22;
            {var subQ0=sQuery(id+"F0.wireOp",EDGE,"E0");var subQ1=makeQuery(id+"F1.opExtrude","SWEPT_FACE",FACE,{"disambiguationData":[OSD([subQ0])]});Q22=makeQuery(id+"F30.boolean.opBoolean","INTERSECT",EDGE,{"derivedFrom":[makeQuery(id+"F3.boolean.opBoolean","SPLIT",FACE,{"disambiguationData":[TD([makeQuery(id+"F1.opExtrude","CAP_FACE",FACE,{"disambiguationData":[OSD([subQ0])],"isStart":true})])],"derivedFrom":subQ1}),makeQuery(id+"F30.opExtrude","SWEPT_FACE",FACE,{"disambiguationData":[OSD([sQuery(id+"F29.wireOp",EDGE,"E5")])]})]});}
            var Q23;
            {var subQ0=sQuery(id+"F4.wireOp",EDGE,"E2");Q23=makeQuery(id+"F30.boolean.opBoolean","INTERSECT",EDGE,{"derivedFrom":[makeQuery(id+"F5.boolean.opBoolean","SPLIT",FACE,{"disambiguationData":[TD([makeQuery(id+"F5.opExtrude","CAP_FACE",FACE,{"disambiguationData":[OSD([subQ0])],"isStart":true})])],"derivedFrom":makeQuery(id+"F5.opExtrude","SWEPT_FACE",FACE,{"disambiguationData":[OSD([subQ0])]})}),makeQuery(id+"F30.opExtrude","SWEPT_FACE",FACE,{"disambiguationData":[OSD([sQuery(id+"F29.wireOp",EDGE,"E5")])]})]});}
            fillet(context, id + "F63", {"entities" : qUnion([Q0, Q1, Q2, Q3, Q4, Q5, Q6, Q7, Q8, Q9, Q10, Q11, Q12, Q13, Q14, Q15, Q16, Q17, Q18, Q19, Q20, Q21, Q22, Q23]), "radius" : 1.5 * mm, "tangentPropagation" : true, "allowEdgeOverflow" : false});
        }
        {
            var Q0;
            {var subQ0=sQuery(id+"F23.wireOp",EDGE,"E3");Q0=makeQuery(id+"F27.boolean.opBoolean","INTERSECT",EDGE,{"derivedFrom":[makeQuery(id+"F24.boolean.opBoolean","SPLIT",FACE,{"disambiguationData":[TD([makeQuery(id+"F24.opExtrude","CAP_FACE",FACE,{"disambiguationData":[OSD([subQ0])],"isStart":false})])],"derivedFrom":makeQuery(id+"F24.opExtrude","SWEPT_FACE",FACE,{"disambiguationData":[OSD([subQ0])]})}),makeQuery(id+"F27.opExtrude","SWEPT_FACE",FACE,{"disambiguationData":[OSD([sQuery(id+"F26.wireOp",EDGE,"E4")])]})]});}
            var Q1;
            {var subQ0=sQuery(id+"F26.wireOp",EDGE,"E4");Q1=makeQuery(id+"F30.boolean.opBoolean","INTERSECT",EDGE,{"derivedFrom":[makeQuery(id+"F27.boolean.opBoolean","SPLIT",FACE,{"disambiguationData":[TD([makeQuery(id+"F27.opExtrude","CAP_FACE",FACE,{"disambiguationData":[OSD([subQ0])],"isStart":true})])],"derivedFrom":makeQuery(id+"F27.opExtrude","SWEPT_FACE",FACE,{"disambiguationData":[OSD([subQ0])]})}),makeQuery(id+"F30.opExtrude","SWEPT_FACE",FACE,{"disambiguationData":[OSD([sQuery(id+"F29.wireOp",EDGE,"E5")])]})]});}
            var Q2;
            {var subQ0=sQuery(id+"F26.wireOp",EDGE,"E4");Q2=makeQuery(id+"F33.boolean.opBoolean","INTERSECT",EDGE,{"derivedFrom":[makeQuery(id+"F27.boolean.opBoolean","SPLIT",FACE,{"disambiguationData":[TD([makeQuery(id+"F27.opExtrude","CAP_FACE",FACE,{"disambiguationData":[OSD([subQ0])],"isStart":true})])],"derivedFrom":makeQuery(id+"F27.opExtrude","SWEPT_FACE",FACE,{"disambiguationData":[OSD([subQ0])]})}),makeQuery(id+"F33.opExtrude","SWEPT_FACE",FACE,{"disambiguationData":[OSD([sQuery(id+"F32.wireOp",EDGE,"E6")])]})]});}
            var Q3;
            {var subQ0=sQuery(id+"F29.wireOp",EDGE,"E5");Q3=makeQuery(id+"F33.boolean.opBoolean","INTERSECT",EDGE,{"derivedFrom":[makeQuery(id+"F30.boolean.opBoolean","SPLIT",FACE,{"disambiguationData":[TD([makeQuery(id+"F30.opExtrude","CAP_FACE",FACE,{"disambiguationData":[OSD([subQ0])],"isStart":true})])],"derivedFrom":makeQuery(id+"F30.opExtrude","SWEPT_FACE",FACE,{"disambiguationData":[OSD([subQ0])]})}),makeQuery(id+"F33.opExtrude","SWEPT_FACE",FACE,{"disambiguationData":[OSD([sQuery(id+"F32.wireOp",EDGE,"E6")])]})]});}
            var Q4;
            {var subQ0=sQuery(id+"F23.wireOp",EDGE,"E3");Q4=makeQuery(id+"F33.boolean.opBoolean","INTERSECT",EDGE,{"derivedFrom":[makeQuery(id+"F24.boolean.opBoolean","SPLIT",FACE,{"disambiguationData":[TD([makeQuery(id+"F24.opExtrude","CAP_FACE",FACE,{"disambiguationData":[OSD([subQ0])],"isStart":false})])],"derivedFrom":makeQuery(id+"F24.opExtrude","SWEPT_FACE",FACE,{"disambiguationData":[OSD([subQ0])]})}),makeQuery(id+"F33.opExtrude","SWEPT_FACE",FACE,{"disambiguationData":[OSD([sQuery(id+"F32.wireOp",EDGE,"E6")])]})]});}
            var Q5;
            {var subQ0=sQuery(id+"F26.wireOp",EDGE,"E4");Q5=makeQuery(id+"F33.boolean.opBoolean","INTERSECT",EDGE,{"derivedFrom":[makeQuery(id+"F27.boolean.opBoolean","SPLIT",FACE,{"disambiguationData":[TD([makeQuery(id+"F27.opExtrude","CAP_FACE",FACE,{"disambiguationData":[OSD([subQ0])],"isStart":false})])],"derivedFrom":makeQuery(id+"F27.opExtrude","SWEPT_FACE",FACE,{"disambiguationData":[OSD([subQ0])]})}),makeQuery(id+"F33.opExtrude","SWEPT_FACE",FACE,{"disambiguationData":[OSD([sQuery(id+"F32.wireOp",EDGE,"E6")])]})]});}
            var Q6;
            {var subQ0=sQuery(id+"F23.wireOp",EDGE,"E3");Q6=makeQuery(id+"F30.boolean.opBoolean","INTERSECT",EDGE,{"derivedFrom":[makeQuery(id+"F24.boolean.opBoolean","SPLIT",FACE,{"disambiguationData":[TD([makeQuery(id+"F24.opExtrude","CAP_FACE",FACE,{"disambiguationData":[OSD([subQ0])],"isStart":true})])],"derivedFrom":makeQuery(id+"F24.opExtrude","SWEPT_FACE",FACE,{"disambiguationData":[OSD([subQ0])]})}),makeQuery(id+"F30.opExtrude","SWEPT_FACE",FACE,{"disambiguationData":[OSD([sQuery(id+"F29.wireOp",EDGE,"E5")])]})]});}
            var Q7;
            {var subQ0=sQuery(id+"F23.wireOp",EDGE,"E3");Q7=makeQuery(id+"F27.boolean.opBoolean","INTERSECT",EDGE,{"derivedFrom":[makeQuery(id+"F24.boolean.opBoolean","SPLIT",FACE,{"disambiguationData":[TD([makeQuery(id+"F24.opExtrude","CAP_FACE",FACE,{"disambiguationData":[OSD([subQ0])],"isStart":true})])],"derivedFrom":makeQuery(id+"F24.opExtrude","SWEPT_FACE",FACE,{"disambiguationData":[OSD([subQ0])]})}),makeQuery(id+"F27.opExtrude","SWEPT_FACE",FACE,{"disambiguationData":[OSD([sQuery(id+"F26.wireOp",EDGE,"E4")])]})]});}
            var Q8;
            {var subQ0=sQuery(id+"F23.wireOp",EDGE,"E3");Q8=makeQuery(id+"F33.boolean.opBoolean","INTERSECT",EDGE,{"derivedFrom":[makeQuery(id+"F24.boolean.opBoolean","SPLIT",FACE,{"disambiguationData":[TD([makeQuery(id+"F24.opExtrude","CAP_FACE",FACE,{"disambiguationData":[OSD([subQ0])],"isStart":true})])],"derivedFrom":makeQuery(id+"F24.opExtrude","SWEPT_FACE",FACE,{"disambiguationData":[OSD([subQ0])]})}),makeQuery(id+"F33.opExtrude","SWEPT_FACE",FACE,{"disambiguationData":[OSD([sQuery(id+"F32.wireOp",EDGE,"E6")])]})]});}
            var Q9;
            {var subQ0=sQuery(id+"F29.wireOp",EDGE,"E5");Q9=makeQuery(id+"F33.boolean.opBoolean","INTERSECT",EDGE,{"derivedFrom":[makeQuery(id+"F30.boolean.opBoolean","SPLIT",FACE,{"disambiguationData":[TD([makeQuery(id+"F30.opExtrude","CAP_FACE",FACE,{"disambiguationData":[OSD([subQ0])],"isStart":false})])],"derivedFrom":makeQuery(id+"F30.opExtrude","SWEPT_FACE",FACE,{"disambiguationData":[OSD([subQ0])]})}),makeQuery(id+"F33.opExtrude","SWEPT_FACE",FACE,{"disambiguationData":[OSD([sQuery(id+"F32.wireOp",EDGE,"E6")])]})]});}
            var Q10;
            {var subQ0=sQuery(id+"F23.wireOp",EDGE,"E3");Q10=makeQuery(id+"F30.boolean.opBoolean","INTERSECT",EDGE,{"derivedFrom":[makeQuery(id+"F24.boolean.opBoolean","SPLIT",FACE,{"disambiguationData":[TD([makeQuery(id+"F24.opExtrude","CAP_FACE",FACE,{"disambiguationData":[OSD([subQ0])],"isStart":false})])],"derivedFrom":makeQuery(id+"F24.opExtrude","SWEPT_FACE",FACE,{"disambiguationData":[OSD([subQ0])]})}),makeQuery(id+"F30.opExtrude","SWEPT_FACE",FACE,{"disambiguationData":[OSD([sQuery(id+"F29.wireOp",EDGE,"E5")])]})]});}
            var Q11;
            {var subQ0=sQuery(id+"F26.wireOp",EDGE,"E4");Q11=makeQuery(id+"F30.boolean.opBoolean","INTERSECT",EDGE,{"derivedFrom":[makeQuery(id+"F27.boolean.opBoolean","SPLIT",FACE,{"disambiguationData":[TD([makeQuery(id+"F27.opExtrude","CAP_FACE",FACE,{"disambiguationData":[OSD([subQ0])],"isStart":false})])],"derivedFrom":makeQuery(id+"F27.opExtrude","SWEPT_FACE",FACE,{"disambiguationData":[OSD([subQ0])]})}),makeQuery(id+"F30.opExtrude","SWEPT_FACE",FACE,{"disambiguationData":[OSD([sQuery(id+"F29.wireOp",EDGE,"E5")])]})]});}
            fillet(context, id + "F64", {"entities" : qUnion([Q0, Q1, Q2, Q3, Q4, Q5, Q6, Q7, Q8, Q9, Q10, Q11]), "radius" : 1.5 * mm, "tangentPropagation" : true, "allowEdgeOverflow" : false});
        }
    });
